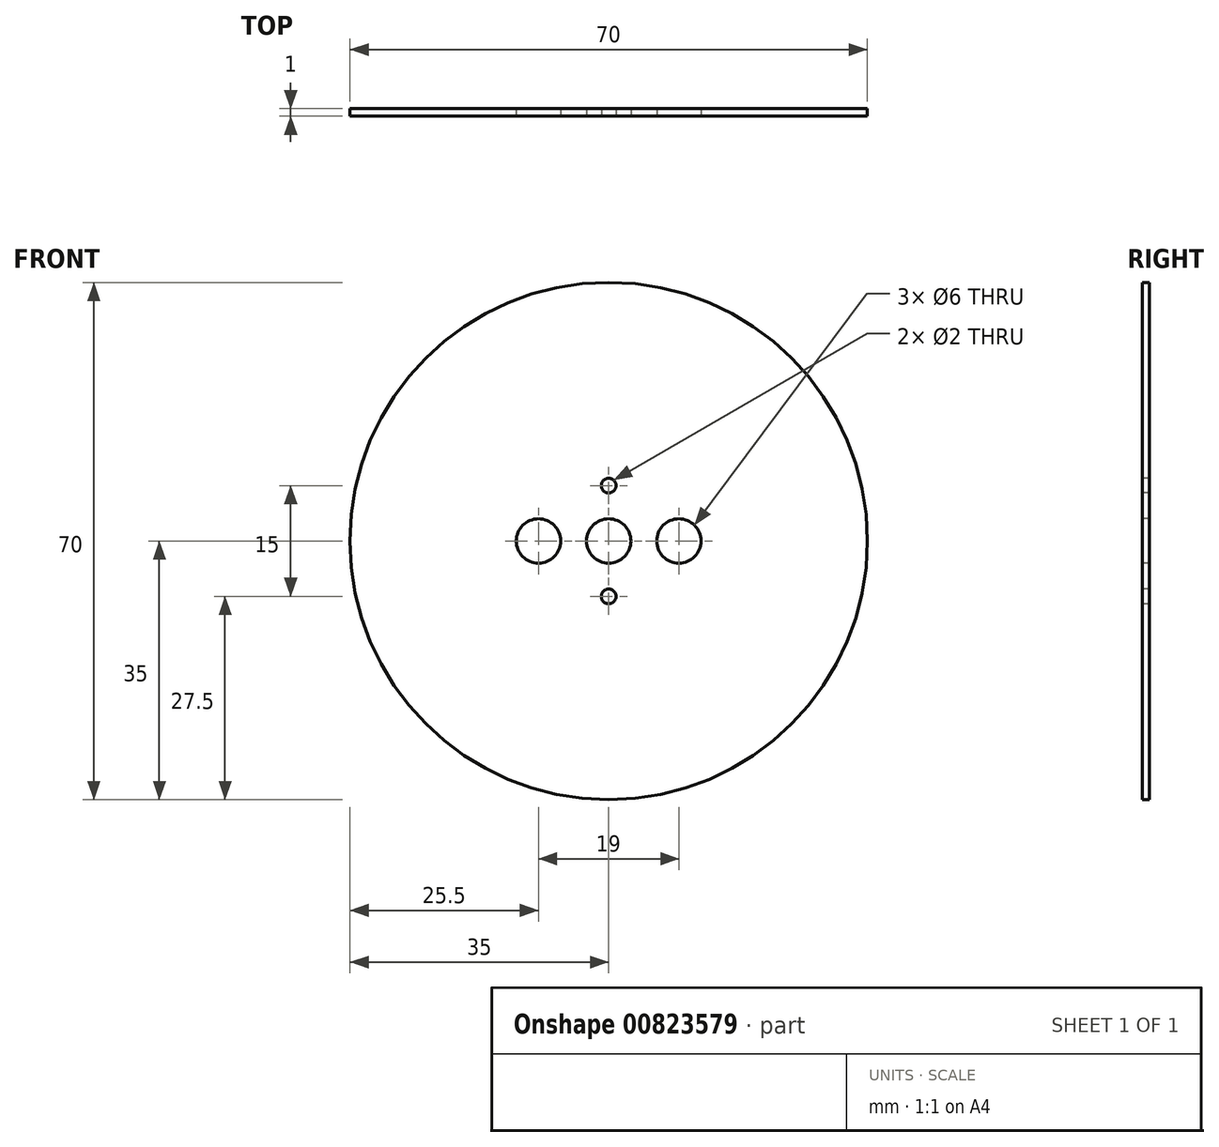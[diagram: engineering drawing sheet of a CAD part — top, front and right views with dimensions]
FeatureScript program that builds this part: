
annotation { "Feature Type Name" : "Feature", "Feature Type Description" : "" }
export const myFeature = defineFeature(function(context is Context, id is Id, definition is map)
    precondition{}
    {
        {
            var Q0;
            Q0=qCreatedBy(makeId("Front.planeOp"),FACE);
            var sketch = newSketch(context, id + "F0", { "sketchPlane" : qUnion([Q0])});
            skCircle(sketch, "E0", {"center": v(0, 0) * mm, "radius": 35 * mm});
            skSolve(sketch);
        }
        {
            var Q0;
            Q0=makeQuery(id+"F0.imprint","IMPRINT",FACE,{"disambiguationData":[TD([[makeQuery(id+"F0.imprint","IMPRINT",EDGE,{"derivedFrom":sQuery(id+"F0.wireOp",EDGE,"E0")}),1.0]])]});
            extrude(context, id + "F1", {"entities" : qUnion([Q0]), "depth" : 1 * mm, "offsetDistance" : 25.4 * mm});
        }
        {
            var Q0;
            Q0=qCreatedBy(makeId("Front.planeOp"),FACE);
            cPlane(context, id + "F2", {"entities" : qUnion([Q0]), "cplaneType" : CPlaneType.OFFSET, "offset" : 4.32 * mm, "width" : 152.4 * mm, "height" : 152.4 * mm});
        }
        {
            var Q0;
            Q0=qCreatedBy(id+"F2.planeOp",FACE);
            var sketch = newSketch(context, id + "F3", { "sketchPlane" : qUnion([Q0])});
            skPoint(sketch, "E1", {"position": v(-9.5, 0) * mm});
            skPoint(sketch, "E2", {"position": v(9.5, 0) * mm});
            skPoint(sketch, "E3", {"position": v(0, -7.5) * mm});
            skPoint(sketch, "E4", {"position": v(0, 7.5) * mm});
            skPoint(sketch, "E5", {"position": v(0, 0) * mm});
            skSolve(sketch);
        }
        {
            var Q0;
            Q0=sQuery(id+"F3.wireOp",VERTEX,"E1");
            var Q1;
            Q1=sQuery(id+"F3.wireOp",VERTEX,"E2");
            var Q2;
            Q2=sQuery(id+"F3.wireOp",VERTEX,"E5");
            var Q3;
            Q3=makeQuery(id+"F1.opExtrude","SWEPT_BODY",BODY,{"disambiguationData":[OSD([sQuery(id+"F0.wireOp",EDGE,"E0")])]});
            hole(context, id + "F4", {"style" : HoleStyle.SIMPLE, "endStyle" : HoleEndStyle.THROUGH, "holeDiameter" : 6 * mm, "majorDiameter" : 5 * mm, "isTappedThrough" : true, "tappedDepth" : 12 * mm, "tapClearance" : 3, "locations" : qUnion([Q0, Q1, Q2]), "scope" : qUnion([Q3])});
        }
        {
            var Q0;
            Q0=sQuery(id+"F3.wireOp",VERTEX,"E4");
            var Q1;
            Q1=sQuery(id+"F3.wireOp",VERTEX,"E3");
            var Q2;
            Q2=makeQuery(id+"F1.opExtrude","SWEPT_BODY",BODY,{"disambiguationData":[OSD([sQuery(id+"F0.wireOp",EDGE,"E0")])]});
            hole(context, id + "F5", {"style" : HoleStyle.SIMPLE, "endStyle" : HoleEndStyle.THROUGH, "holeDiameter" : 2 * mm, "majorDiameter" : 5 * mm, "isTappedThrough" : true, "tappedDepth" : 12 * mm, "tapClearance" : 3, "locations" : qUnion([Q0, Q1]), "scope" : qUnion([Q2])});
        }
    });
